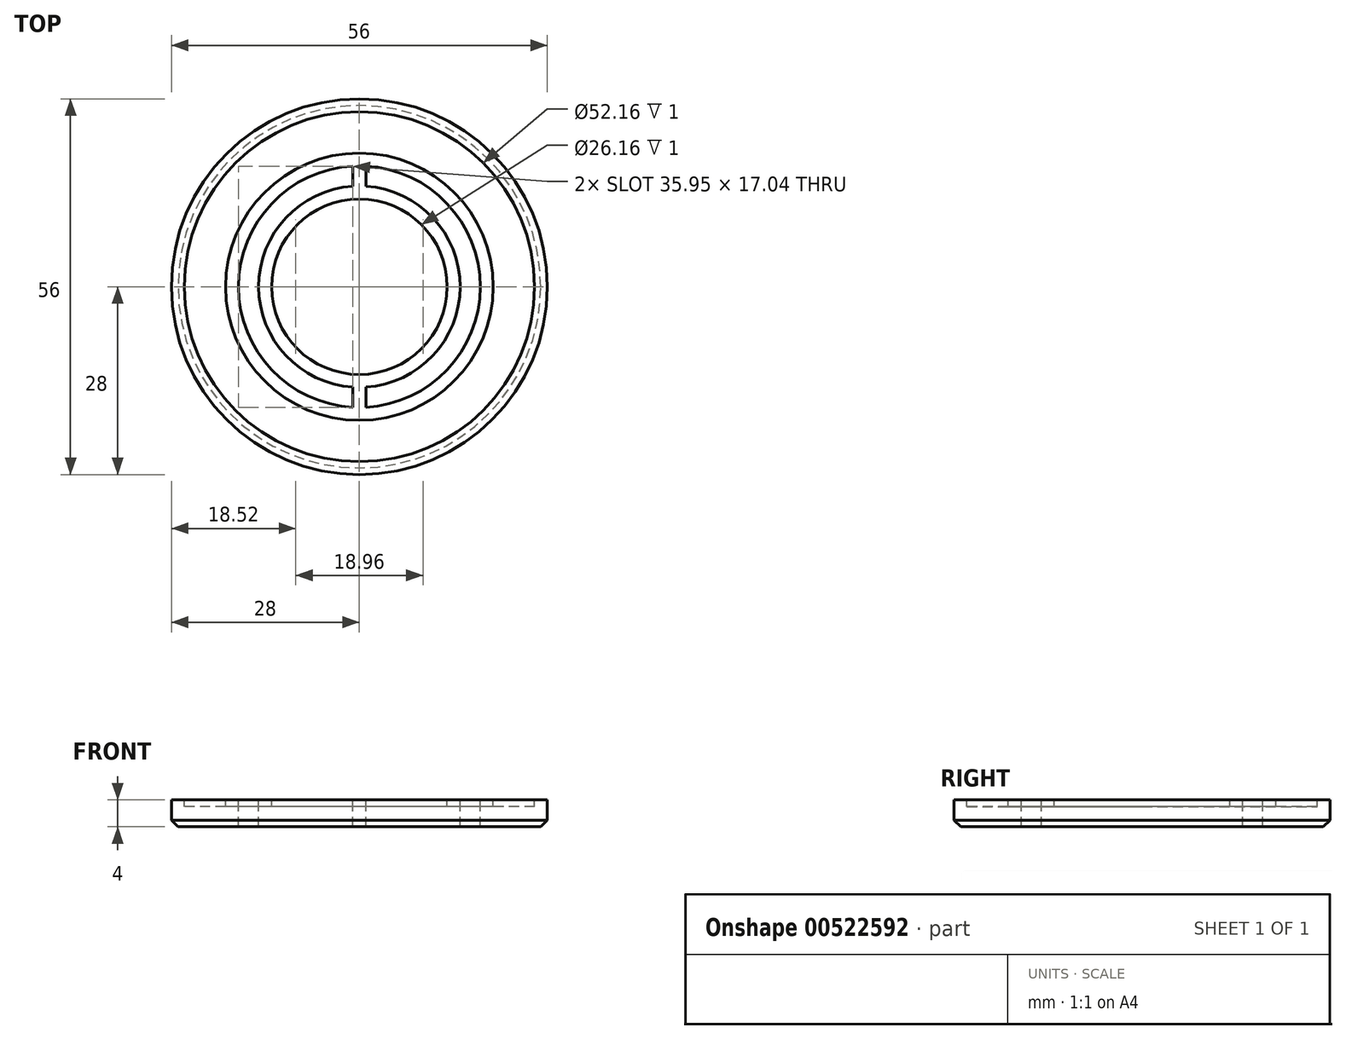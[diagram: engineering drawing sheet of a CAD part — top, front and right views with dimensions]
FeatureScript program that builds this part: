
annotation { "Feature Type Name" : "Feature", "Feature Type Description" : "" }
export const myFeature = defineFeature(function(context is Context, id is Id, definition is map)
    precondition{}
    {
        {
            var Q0;
            Q0=qCreatedBy(makeId("Top.planeOp"),FACE);
            var sketch = newSketch(context, id + "F0", { "sketchPlane" : qUnion([Q0])});
            skCircle(sketch, "E0", {"center": v(0, 0) * mm, "radius": 28 * mm});
            skSolve(sketch);
        }
        {
            var Q0;
            Q0=makeQuery(id+"F0.imprint","IMPRINT",FACE,{"disambiguationData":[TD([[makeQuery(id+"F0.imprint","IMPRINT",EDGE,{"derivedFrom":sQuery(id+"F0.wireOp",EDGE,"E0")}),1.0]])]});
            extrude(context, id + "F1", {"entities" : qUnion([Q0]), "depth" : 4 * mm, "offsetDistance" : 25 * mm});
        }
        {
            var Q0;
            Q0=makeQuery(id+"F1.opExtrude","CAP_FACE",FACE,{"disambiguationData":[OSD([sQuery(id+"F0.wireOp",EDGE,"E0")])],"isStart":false});
            var sketch = newSketch(context, id + "F2", { "sketchPlane" : qUnion([Q0])});
            skCircle(sketch, "E1", {"center": v(0, 0) * mm, "radius": 15 * mm});
            skCircle(sketch, "E2", {"center": v(0, 0) * mm, "radius": 18 * mm});
            skLineSegment(sketch, "E3", {"start": v(0, 15) * mm, "end": v(0, 18) * mm, "construction": true});
            skPoint(sketch, "E4", {"position": v(0, 16.5) * mm});
            skLineSegment(sketch, "E5", {"start": v(0, 16.5) * mm, "end": v(0.96, 16.5) * mm, "construction": true});
            skLineSegment(sketch, "E6.MirrorCS", {"start": v(0, 16.5) * mm, "end": v(-0.96, 16.5) * mm, "construction": true});
            skLineSegment(sketch, "E7", {"start": v(0.96, 17.97) * mm, "end": v(0.96, 14.97) * mm});
            skLineSegment(sketch, "E8", {"start": v(-0.96, 17.97) * mm, "end": v(-0.96, 14.97) * mm});
            skLineSegment(sketch, "E9", {"start": v(-15, 0) * mm, "end": v(15, 0) * mm, "construction": true});
            skLineSegment(sketch, "E10.MirrorCS", {"start": v(-0.96, -17.97) * mm, "end": v(-0.96, -14.97) * mm});
            skLineSegment(sketch, "E11.MirrorCS", {"start": v(0.96, -17.97) * mm, "end": v(0.96, -14.97) * mm});
            skSolve(sketch);
        }
        {
            var Q0;
            {var subQ0=sQuery(id+"F2.wireOp",EDGE,"E8");Q0=makeQuery(id+"F2.imprint","IMPRINT",FACE,{"disambiguationData":[TD([[makeQuery(id+"F2.imprint","IMPRINT",EDGE,{"derivedFrom":subQ0}),-1.0]])]});}
            var Q1;
            {var subQ0=sQuery(id+"F2.wireOp",EDGE,"E7");Q1=makeQuery(id+"F2.imprint","IMPRINT",FACE,{"disambiguationData":[TD([[makeQuery(id+"F2.imprint","IMPRINT",EDGE,{"derivedFrom":subQ0}),1.0]])]});}
            extrude(context, id + "F3", {"entities" : qUnion([Q0, Q1]), "operationType" : NewBodyOperationType.REMOVE, "endBound" : BoundingType.UP_TO_NEXT, "oppositeDirection" : true, "depth" : 25 * mm, "offsetDistance" : 25 * mm});
        }
        {
            var Q0;
            Q0=makeQuery(id+"F1.opExtrude","CAP_FACE",FACE,{"disambiguationData":[OSD([sQuery(id+"F0.wireOp",EDGE,"E0")])],"isStart":false});
            var sketch = newSketch(context, id + "F4", { "sketchPlane" : qUnion([Q0])});
            skCircle(sketch, "E12", {"center": v(0, 0) * mm, "radius": 26.08 * mm});
            skCircle(sketch, "E13", {"center": v(0, 0) * mm, "radius": 19.92 * mm});
            skCircle(sketch, "E14", {"center": v(0, 0) * mm, "radius": 13.08 * mm});
            skSolve(sketch);
        }
        {
            var Q0;
            Q0=makeQuery(id+"F4.imprint","IMPRINT",FACE,{"disambiguationData":[TD([[makeQuery(id+"F4.imprint","IMPRINT",EDGE,{"derivedFrom":sQuery(id+"F4.wireOp",EDGE,"E12")}),1.0]])]});
            var Q1;
            Q1=makeQuery(id+"F4.imprint","IMPRINT",FACE,{"disambiguationData":[TD([[makeQuery(id+"F4.imprint","IMPRINT",EDGE,{"derivedFrom":sQuery(id+"F4.wireOp",EDGE,"E14")}),1.0]])]});
            extrude(context, id + "F5", {"entities" : qUnion([Q0, Q1]), "operationType" : NewBodyOperationType.REMOVE, "oppositeDirection" : true, "depth" : 1 * mm, "offsetDistance" : 25 * mm});
        }
        {
            var Q0;
            Q0=makeQuery(id+"F1.opExtrude","CAP_EDGE",EDGE,{"disambiguationData":[OSD([sQuery(id+"F0.wireOp",EDGE,"E0")])],"isStart":true});
            chamfer(context, id + "F6", {"entities" : qUnion([Q0]), "width" : 1 * mm, "tangentPropagation" : true});
        }
    });
